# Revit family: 2NaughtOne_Mimo2-PositionModular
name_source: partatom
category: Furniture
units: mm (PartAtom-declared; Revit-internal decimal feet)

## family parameters
Always vertical = Yes
Cut with Voids When Loaded = No
OmniClass Number = 23.40.70.14.64.14
OmniClass Title = Retail and Commercial Seating Furniture
Room Calculation Point = No
Shared = No
Work Plane-Based = No

## types (1)
- Ottoman Seat with Back
    Assembly Code = E2010200
    Brand = NaughtOne
    Default Elevation = 0 "
    Description = Mimo 2 Position Modular Ottoman Seat with Back
    Left Arm = No
    Left Back = Yes
    Left Seat = Yes
    Manufacturer = MillerKnoll, Inc.
    Model = NOMMO2BO
    Package Qty = 1
    Right Arm = No
    Right Back = No
    Right Seat = No
    Tag = NOMMO2BO
    Type = 1
    Type 1 = Yes
    Type 2 = No
    Type 3 = No
    Type 4 = No
    Type 5 = No
    URL = https://www.naughtone.com

## geometry (parser evidence)
native form markers: Sweep x11
no freeform markers — native parametric forms only
